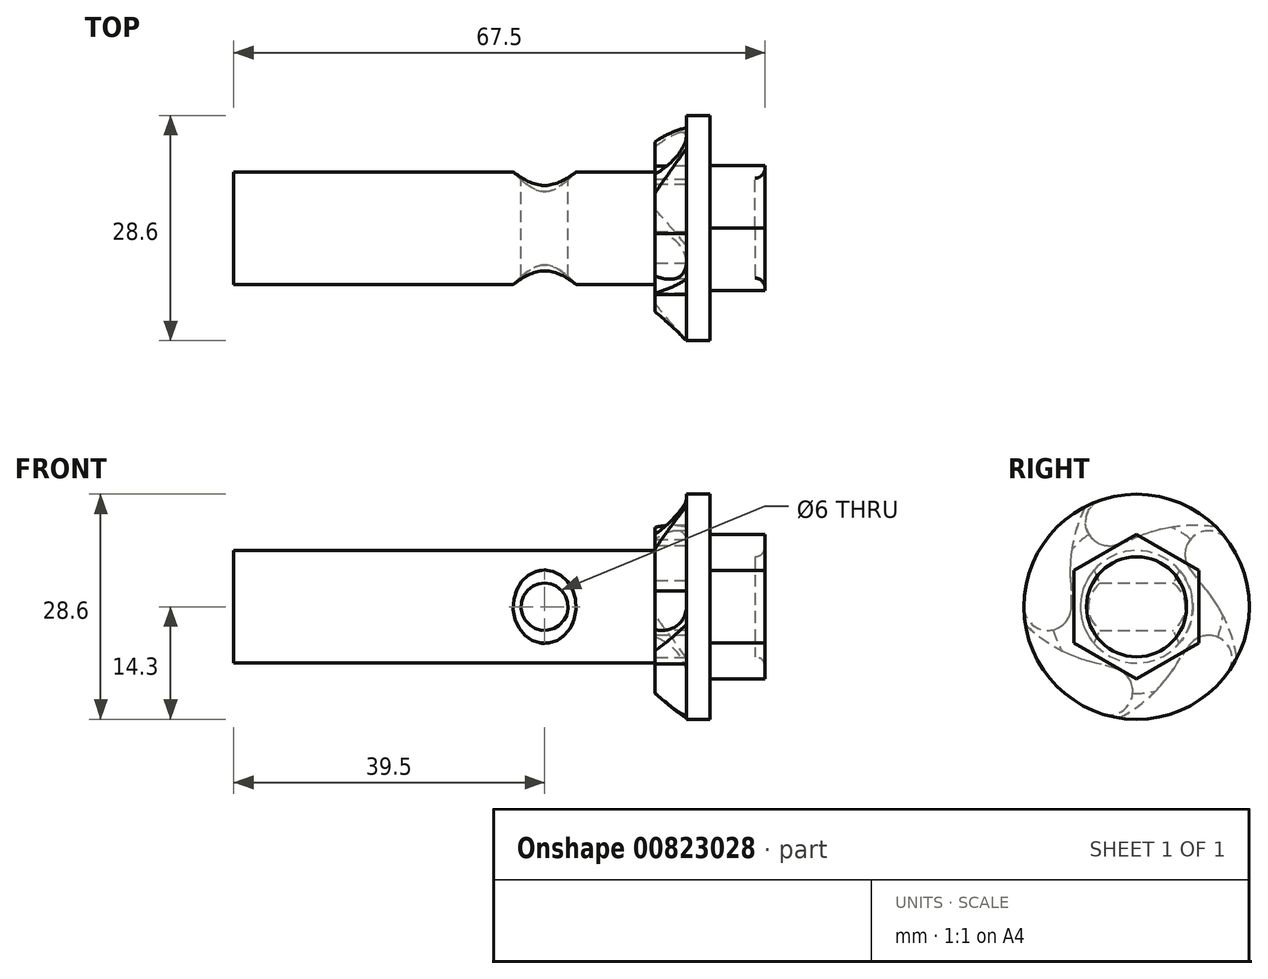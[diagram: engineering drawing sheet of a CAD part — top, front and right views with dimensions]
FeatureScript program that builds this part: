
annotation { "Feature Type Name" : "Feature", "Feature Type Description" : "" }
export const myFeature = defineFeature(function(context is Context, id is Id, definition is map)
    precondition{}
    {
        {
            var Q0;
            Q0=qCreatedBy(makeId("Front.planeOp"),FACE);
            var sketch = newSketch(context, id + "F0", { "sketchPlane" : qUnion([Q0])});
            skLineSegment(sketch, "E0", {"start": v(0, 0) * mm, "end": v(0, 7.14) * mm, "construction": true});
            skLineSegment(sketch, "E1", {"start": v(0, 7.14) * mm, "end": v(-53.5, 7.14) * mm});
            skLineSegment(sketch, "E2", {"start": v(-53.5, 7.14) * mm, "end": v(-53.5, 0) * mm});
            skLineSegment(sketch, "E3", {"start": v(-53.5, 0) * mm, "end": v(0, 0) * mm});
            skLineSegment(sketch, "E4", {"start": v(0, 7.14) * mm, "end": v(0, 11) * mm});
            skLineSegment(sketch, "E5", {"start": v(4, 14.3) * mm, "end": v(7, 14.3) * mm});
            skLineSegment(sketch, "E6", {"start": v(7, 14.3) * mm, "end": v(7, 10) * mm});
            skLineSegment(sketch, "E7", {"start": v(7, 10) * mm, "end": v(14, 10) * mm});
            skLineSegment(sketch, "E8", {"start": v(14, 10) * mm, "end": v(14, 6.35) * mm});
            skLineSegment(sketch, "E9", {"start": v(12.7, 0) * mm, "end": v(0, 0) * mm});
            skLineSegment(sketch, "E10", {"start": v(12.7, 0) * mm, "end": v(12.7, 6.35) * mm});
            skLineSegment(sketch, "E11", {"start": v(12.7, 6.35) * mm, "end": v(14, 6.35) * mm});
            skPoint(sketch, "E12.orphan", {"position": v(14, 0) * mm});
            skLineSegment(sketch, "E13", {"start": v(4, 14.3) * mm, "end": v(0, 11) * mm});
            skSolve(sketch);
        }
        {
            var Q0;
            Q0=qSketchRegion(id+"F0",true);
            var Q1;
            Q1=sQuery(id+"F0.wireOp",EDGE,"E3");
            revolve(context, id + "F1", {"surfaceOperationType" : NewSurfaceOperationType.NEW, "entities" : qUnion([Q0]), "axis" : qUnion([Q1]), "revolveType" : RevolveType.FULL});
        }
        {
            var Q0;
            Q0=makeQuery(id+"F1.opRevolve","SWEPT_FACE",FACE,{"disambiguationData":[OSD([sQuery(id+"F0.wireOp",EDGE,"E8")])]});
            var sketch = newSketch(context, id + "F2", { "sketchPlane" : qUnion([Q0])});
            skCircle(sketch, "E14.cCircle", {"center": v(0, 0) * mm, "radius": 7.94 * mm, "construction": true});
            skLineSegment(sketch, "E14.0", {"start": v(-7.94, -4.58) * mm, "end": v(-7.94, 4.58) * mm});
            skLineSegment(sketch, "E14.1", {"start": v(-7.94, 4.58) * mm, "end": v(0, 9.17) * mm});
            skLineSegment(sketch, "E14.2", {"start": v(0, 9.17) * mm, "end": v(7.94, 4.58) * mm});
            skLineSegment(sketch, "E14.3", {"start": v(7.94, 4.58) * mm, "end": v(7.94, -4.58) * mm});
            skLineSegment(sketch, "E14.4", {"start": v(7.94, -4.58) * mm, "end": v(0, -9.17) * mm});
            skLineSegment(sketch, "E14.5", {"start": v(0, -9.17) * mm, "end": v(-7.94, -4.58) * mm});
            skPoint(sketch, "E14.0.midPoint", {"position": v(-7.94, 0) * mm});
            skCircle(sketch, "E15", {"center": v(0, 0) * mm, "radius": 11.06 * mm});
            skSolve(sketch);
        }
        {
            var Q0;
            Q0=qSketchRegion(id+"F2",true);
            var Q1;
            Q1=makeQuery(id+"F1.opRevolve","SWEPT_FACE",FACE,{"disambiguationData":[OSD([sQuery(id+"F0.wireOp",EDGE,"E6")])]});
            extrude(context, id + "F3", {"entities" : qUnion([Q0]), "operationType" : NewBodyOperationType.REMOVE, "endBound" : BoundingType.UP_TO_SURFACE, "oppositeDirection" : true, "depth" : 25 * mm, "endBoundEntityFace" : qUnion([Q1]), "offsetDistance" : 25 * mm});
        }
        {
            var Q0;
            Q0=makeQuery(id+"F1.opRevolve","SWEPT_EDGE",EDGE,{"disambiguationData":[OSD([sQuery(id+"F0.wireOp",EDGE,"E8"),sQuery(id+"F0.wireOp",EDGE,"E11")])]});
            fillet(context, id + "F4", {"entities" : qUnion([Q0]), "radius" : 1.3 * mm, "tangentPropagation" : true, "allowEdgeOverflow" : false});
        }
        {
            var Q0;
            Q0=makeQuery(id+"F1.opRevolve","SWEPT_FACE",FACE,{"disambiguationData":[OSD([sQuery(id+"F0.wireOp",EDGE,"E4")])]});
            var sketch = newSketch(context, id + "F5", { "sketchPlane" : qUnion([Q0])});
            skLineSegment(sketch, "E16", {"start": v(0, 0) * mm, "end": v(6.51, 12.73) * mm, "construction": true});
            skCircle(sketch, "E17.0", {"center": v(0, 0) * mm, "radius": 14.3 * mm, "construction": true});
            skLineSegment(sketch, "E18", {"start": v(0, 0) * mm, "end": v(14.3, 0) * mm, "construction": true});
            skLineSegment(sketch, "E19", {"start": v(14.3, 0) * mm, "end": v(8.3, 0) * mm, "construction": true});
            skArc(sketch, "E20", {"start": v(8.3, 0) * mm, "mid": v(11.3, -3) * mm, "end": v(14.3, 0) * mm});
            skLineSegment(sketch, "E21", {"start": v(8.3, 0) * mm, "end": v(8.3, 2) * mm});
            skArc(sketch, "E22", {"start": v(8.3, 2) * mm, "mid": v(8.2, 7.5) * mm, "end": v(6.51, 12.73) * mm});
            skLineSegment(sketch, "E23", {"start": v(14.3, 0) * mm, "end": v(16.26, 0) * mm});
            skLineSegment(sketch, "E24", {"start": v(16.26, 0) * mm, "end": v(16.26, 14.17) * mm});
            skLineSegment(sketch, "E25", {"start": v(16.26, 14.17) * mm, "end": v(6.51, 14.25) * mm});
            skLineSegment(sketch, "E26", {"start": v(6.51, 14.25) * mm, "end": v(6.51, 12.73) * mm});
            skLineSegment(sketch, "E27.1.0", {"start": v(-11.54, 10.6) * mm, "end": v(-10.1, 10.13) * mm});
            skLineSegment(sketch, "E27.1.1", {"start": v(-8.45, 19.84) * mm, "end": v(-11.54, 10.6) * mm});
            skArc(sketch, "E27.1.2", {"start": v(2.56, 7.9) * mm, "mid": v(6.35, 9.82) * mm, "end": v(4.42, 13.6) * mm});
            skLineSegment(sketch, "E27.1.3", {"start": v(2.56, 7.9) * mm, "end": v(0.66, 8.51) * mm});
            skLineSegment(sketch, "E27.1.4", {"start": v(5.03, 15.47) * mm, "end": v(-8.45, 19.84) * mm});
            skLineSegment(sketch, "E27.1.5", {"start": v(4.42, 13.6) * mm, "end": v(5.03, 15.47) * mm});
            skArc(sketch, "E27.1.6", {"start": v(0.66, 8.51) * mm, "mid": v(-4.6, 10.12) * mm, "end": v(-10.1, 10.13) * mm});
            skLineSegment(sketch, "E27.2.0", {"start": v(-13.64, -7.7) * mm, "end": v(-12.75, -6.47) * mm});
            skLineSegment(sketch, "E27.2.1", {"start": v(-21.48, -1.9) * mm, "end": v(-13.64, -7.7) * mm});
            skArc(sketch, "E27.2.2", {"start": v(-6.71, 4.88) * mm, "mid": v(-7.38, 9.07) * mm, "end": v(-11.57, 8.4) * mm});
            skLineSegment(sketch, "E27.2.3", {"start": v(-6.71, 4.88) * mm, "end": v(-7.9, 3.26) * mm});
            skLineSegment(sketch, "E27.2.4", {"start": v(-13.16, 9.56) * mm, "end": v(-21.48, -1.9) * mm});
            skLineSegment(sketch, "E27.2.5", {"start": v(-11.57, 8.4) * mm, "end": v(-13.16, 9.56) * mm});
            skArc(sketch, "E27.2.6", {"start": v(-7.9, 3.26) * mm, "mid": v(-11.05, -1.24) * mm, "end": v(-12.75, -6.47) * mm});
            skLineSegment(sketch, "E27.3.0", {"start": v(3.1, -15.35) * mm, "end": v(2.22, -14.13) * mm});
            skLineSegment(sketch, "E27.3.1", {"start": v(-4.83, -21.02) * mm, "end": v(3.1, -15.35) * mm});
            skArc(sketch, "E27.3.2", {"start": v(-6.71, -4.88) * mm, "mid": v(-10.9, -4.21) * mm, "end": v(-11.57, -8.4) * mm});
            skLineSegment(sketch, "E27.3.3", {"start": v(-6.71, -4.88) * mm, "end": v(-5.54, -6.5) * mm});
            skLineSegment(sketch, "E27.3.4", {"start": v(-13.16, -9.56) * mm, "end": v(-4.83, -21.02) * mm});
            skLineSegment(sketch, "E27.3.5", {"start": v(-11.57, -8.4) * mm, "end": v(-13.16, -9.56) * mm});
            skArc(sketch, "E27.3.6", {"start": v(-5.54, -6.5) * mm, "mid": v(-2.23, -10.89) * mm, "end": v(2.22, -14.13) * mm});
            skLineSegment(sketch, "E27.4.0", {"start": v(15.56, -1.79) * mm, "end": v(14.12, -2.26) * mm});
            skLineSegment(sketch, "E27.4.1", {"start": v(18.5, -11.09) * mm, "end": v(15.56, -1.79) * mm});
            skArc(sketch, "E27.4.2", {"start": v(2.56, -7.9) * mm, "mid": v(0.64, -11.67) * mm, "end": v(4.42, -13.6) * mm});
            skLineSegment(sketch, "E27.4.3", {"start": v(2.56, -7.9) * mm, "end": v(4.47, -7.28) * mm});
            skLineSegment(sketch, "E27.4.4", {"start": v(5.03, -15.47) * mm, "end": v(18.5, -11.09) * mm});
            skLineSegment(sketch, "E27.4.5", {"start": v(4.42, -13.6) * mm, "end": v(5.03, -15.47) * mm});
            skArc(sketch, "E27.4.6", {"start": v(4.47, -7.28) * mm, "mid": v(9.67, -5.49) * mm, "end": v(14.12, -2.26) * mm});
            skSolve(sketch);
        }
        {
            var Q0;
            Q0=qSketchRegion(id+"F5",true);
            extrude(context, id + "F6", {"entities" : qUnion([Q0]), "operationType" : NewBodyOperationType.REMOVE, "oppositeDirection" : true, "depth" : 4 * mm, "offsetDistance" : 25 * mm});
        }
        {
            var Q0;
            Q0=qCreatedBy(makeId("Front.planeOp"),FACE);
            var sketch = newSketch(context, id + "F7", { "sketchPlane" : qUnion([Q0])});
            skLineSegment(sketch, "E28", {"start": v(0, 0) * mm, "end": v(-14, 0) * mm, "construction": true});
            skCircle(sketch, "E29", {"center": v(-14, 0) * mm, "radius": 3 * mm});
            skSolve(sketch);
        }
        {
            var Q0;
            Q0=qSketchRegion(id+"F7",true);
            extrude(context, id + "F8", {"entities" : qUnion([Q0]), "operationType" : NewBodyOperationType.REMOVE, "endBound" : BoundingType.SYMMETRIC, "depth" : 25 * mm, "offsetDistance" : 25 * mm});
        }
        {
            var Q0;
            Q0=makeQuery(id+"F8.boolean.opBoolean","COPY",FACE,{"derivedFrom":makeQuery(id+"F8.opExtrude","SWEPT_FACE",FACE,{"disambiguationData":[OSD([sQuery(id+"F7.wireOp",EDGE,"E29")])]})});
            chamfer(context, id + "F9", {"entities" : qUnion([Q0]), "width" : 1 * mm, "tangentPropagation" : true});
        }
    });
